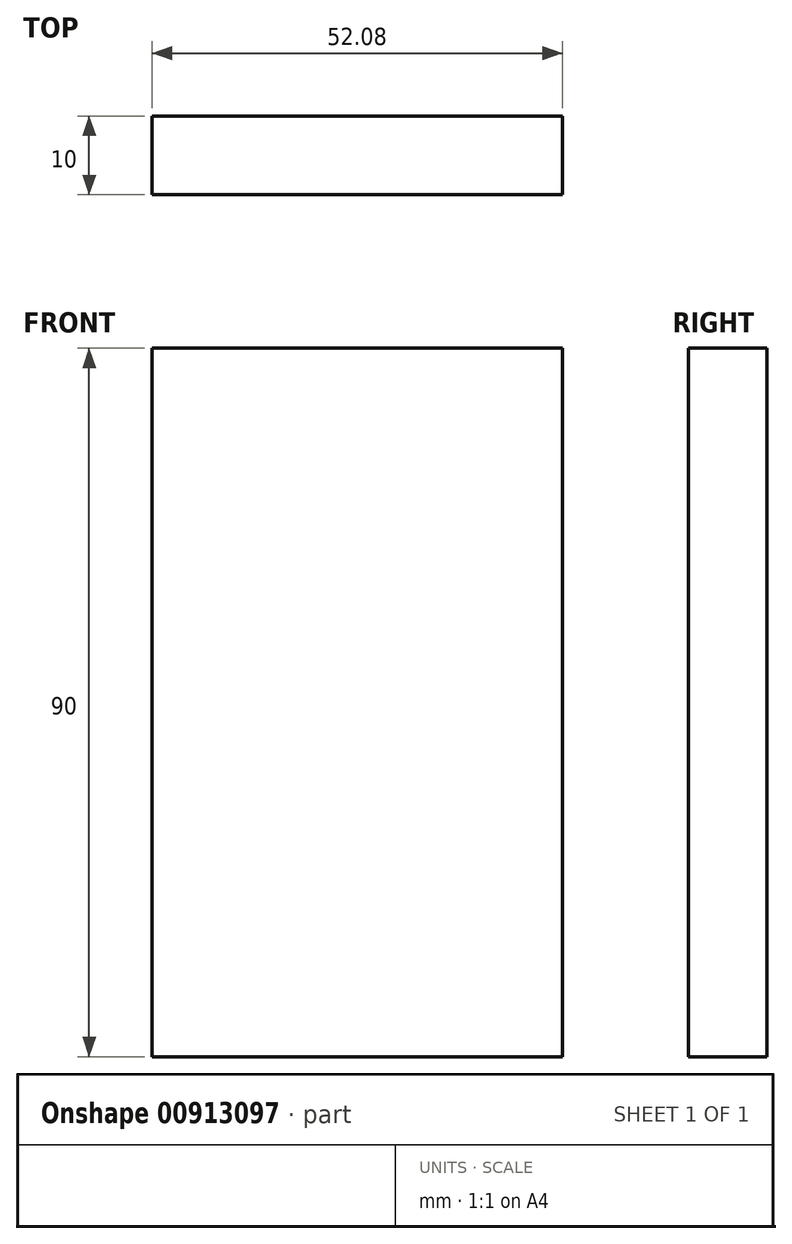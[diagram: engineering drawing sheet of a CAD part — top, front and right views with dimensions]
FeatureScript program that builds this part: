
annotation { "Feature Type Name" : "Feature", "Feature Type Description" : "" }
export const myFeature = defineFeature(function(context is Context, id is Id, definition is map)
    precondition{}
    {
        {
            var Q0;
            Q0=qCreatedBy(makeId("Front.planeOp"),FACE);
            var sketch = newSketch(context, id + "F0", { "sketchPlane" : qUnion([Q0])});
            skLineSegment(sketch, "E0.bottom", {"start": v(26.04, -45) * mm, "end": v(-26.05, -45) * mm});
            skLineSegment(sketch, "E0.top", {"start": v(26.04, 45) * mm, "end": v(-26.04, 45) * mm});
            skLineSegment(sketch, "E0.left", {"start": v(26.04, -45) * mm, "end": v(26.04, 45) * mm});
            skLineSegment(sketch, "E0.right", {"start": v(-26.05, -45) * mm, "end": v(-26.05, 45) * mm});
            skPoint(sketch, "E0.middle", {"position": v(0, 0) * mm});
            skSolve(sketch);
        }
        {
            var Q0;
            Q0 = qSketchRegion(id + "F0", true);
            extrude(context, id + "F1", {"entities" : qUnion([Q0]), "depth" : 10 * mm, "offsetDistance" : 25 * mm});
        }
    });
